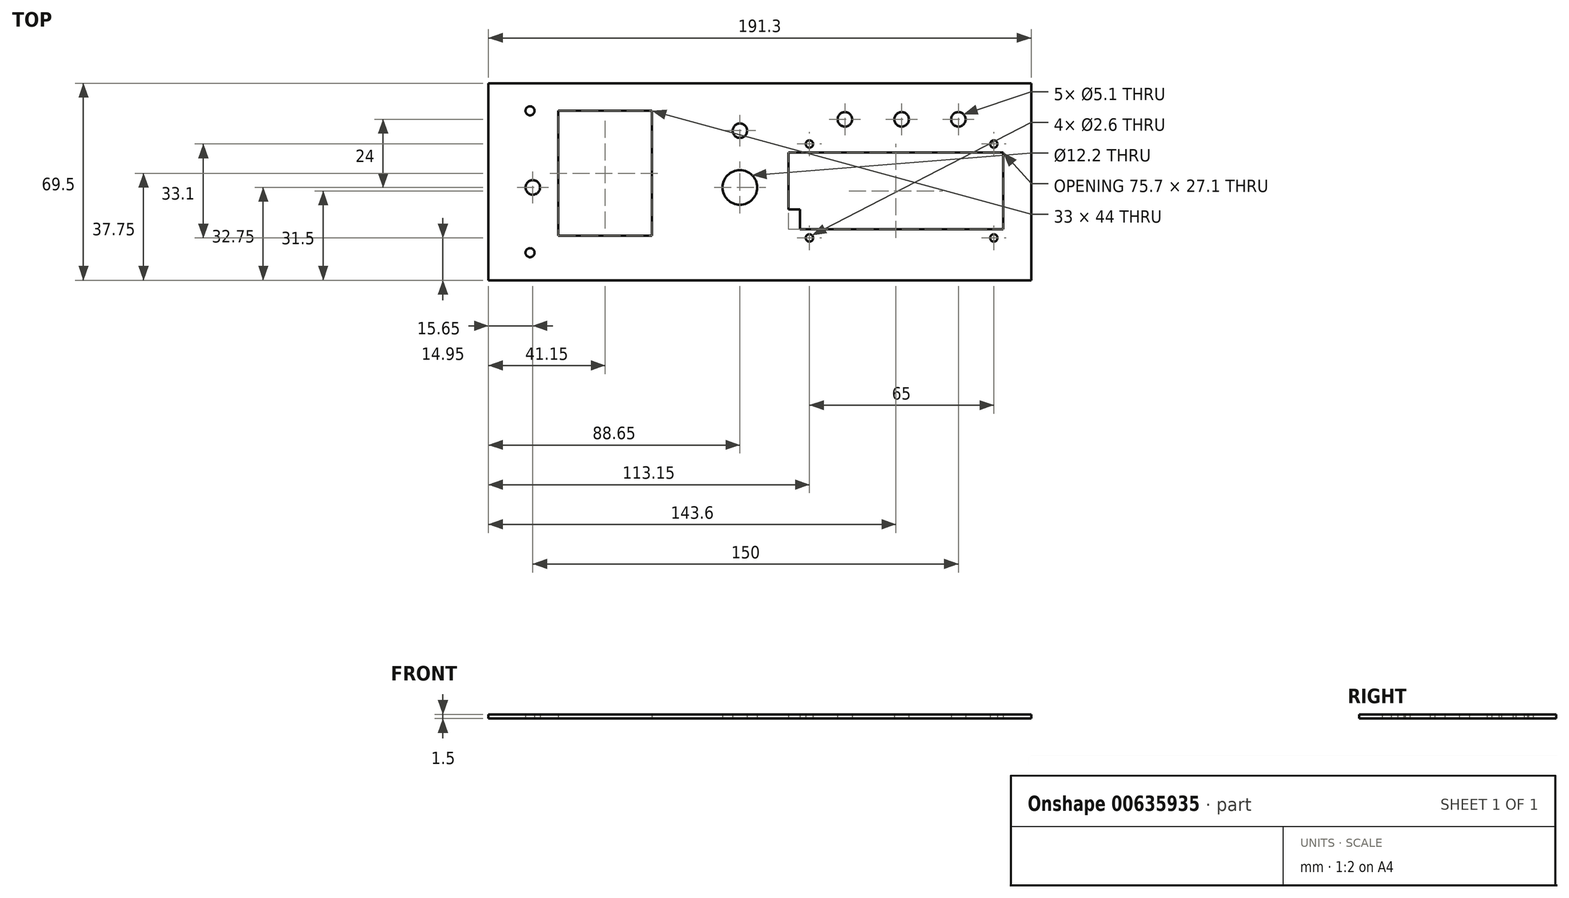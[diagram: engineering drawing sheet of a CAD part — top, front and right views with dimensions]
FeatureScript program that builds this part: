
annotation { "Feature Type Name" : "Feature", "Feature Type Description" : "" }
export const myFeature = defineFeature(function(context is Context, id is Id, definition is map)
    precondition{}
    {
        {
            var Q0;
            Q0=qCreatedBy(makeId("Top.planeOp"),FACE);
            var sketch = newSketch(context, id + "F0", { "sketchPlane" : qUnion([Q0])});
            skLineSegment(sketch, "E0.bottom", {"start": v(-5.65, -4.75) * mm, "end": v(185.65, -4.75) * mm});
            skLineSegment(sketch, "E0.top", {"start": v(-5.65, 64.75) * mm, "end": v(185.65, 64.75) * mm});
            skLineSegment(sketch, "E0.left", {"start": v(-5.65, -4.75) * mm, "end": v(-5.65, 64.75) * mm});
            skLineSegment(sketch, "E0.right", {"start": v(185.65, -4.75) * mm, "end": v(185.65, 64.75) * mm});
            skCircle(sketch, "E1", {"center": v(9, 55) * mm, "radius": 1.6 * mm});
            skCircle(sketch, "E2", {"center": v(10, 28) * mm, "radius": 2.55 * mm});
            skCircle(sketch, "E3", {"center": v(9, 5) * mm, "radius": 1.6 * mm});
            skCircle(sketch, "E4", {"center": v(83, 48) * mm, "radius": 2.55 * mm});
            skCircle(sketch, "E5", {"center": v(83, 28) * mm, "radius": 6.1 * mm});
            skCircle(sketch, "E6", {"center": v(120, 52) * mm, "radius": 2.55 * mm});
            skCircle(sketch, "E7", {"center": v(140, 52) * mm, "radius": 2.55 * mm});
            skCircle(sketch, "E8", {"center": v(160, 52) * mm, "radius": 2.55 * mm});
            skCircle(sketch, "E9", {"center": v(107.5, 10.2) * mm, "radius": 1.3 * mm});
            skCircle(sketch, "E10", {"center": v(172.5, 10.2) * mm, "radius": 1.3 * mm});
            skCircle(sketch, "E11", {"center": v(107.5, 43.3) * mm, "radius": 1.3 * mm});
            skCircle(sketch, "E12", {"center": v(172.5, 43.3) * mm, "radius": 1.3 * mm});
            skLineSegment(sketch, "E13.bottom", {"start": v(104.2, 13.2) * mm, "end": v(175.8, 13.2) * mm});
            skLineSegment(sketch, "E13.top", {"start": v(104.2, 40.3) * mm, "end": v(175.8, 40.3) * mm});
            skLineSegment(sketch, "E13.left", {"start": v(104.2, 13.2) * mm, "end": v(104.2, 20.3) * mm});
            skLineSegment(sketch, "E13.right", {"start": v(175.8, 13.2) * mm, "end": v(175.8, 40.3) * mm});
            skLineSegment(sketch, "E14.bottom", {"start": v(19, 11) * mm, "end": v(52, 11) * mm});
            skLineSegment(sketch, "E14.top", {"start": v(19, 55) * mm, "end": v(52, 55) * mm});
            skLineSegment(sketch, "E14.left", {"start": v(19, 11) * mm, "end": v(19, 55) * mm});
            skLineSegment(sketch, "E14.right", {"start": v(52, 11) * mm, "end": v(52, 55) * mm});
            skLineSegment(sketch, "E15.bottom", {"start": v(104.2, 40.3) * mm, "end": v(100.1, 40.3) * mm});
            skLineSegment(sketch, "E15.top", {"start": v(104.2, 20.3) * mm, "end": v(100.1, 20.3) * mm});
            skLineSegment(sketch, "E15.right", {"start": v(100.1, 40.3) * mm, "end": v(100.1, 20.3) * mm});
            skPoint(sketch, "E16", {"position": v(38, 50) * mm});
            skSolve(sketch);
        }
        {
            var Q0;
            Q0=makeQuery(id+"F0.imprint","IMPRINT",FACE,{"disambiguationData":[TD([[makeQuery(id+"F0.imprint","IMPRINT",EDGE,{"derivedFrom":sQuery(id+"F0.wireOp",EDGE,"E0.bottom")}),1.0]])]});
            extrude(context, id + "F1", {"entities" : qUnion([Q0]), "depth" : 1.5 * mm, "offsetDistance" : 25 * mm});
        }
    });
